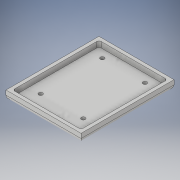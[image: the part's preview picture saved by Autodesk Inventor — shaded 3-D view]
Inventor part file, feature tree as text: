
AUTODESK INVENTOR PART (.ipt)
format: ipt  version: 2019.4 (Build 234330000, 330)  size: 144,384 bytes
history: native  units: mm
features: extrude x3, sketch x3, fillet x2
ambient origin geometry x8: Origin, YZ Plane, XZ Plane, XY Plane, X Axis, Y Axis, Z Axis, Center Point
bodies: Solid1 (feature_tree)
feature tree (8):
  extrude  "Extrusion1"  Depth=83.0mm
  extrude  "Extrusion2"  Depth=61.0mm
  extrude  "Extrusion3"  Depth=5.0mm TaperAngle=0.0deg
  fillet  "Fillet1"  Radius=3.5mm
  fillet  "Fillet2"  Radius=7.5mm
  sketch  "Sketch1"  dims[d0=67.0mm d1=83.0mm]
  sketch  "Sketch2"  dims[d2=3.0mm d3=0.0mm d4=61.0mm]
  sketch  "Sketch3"  dims[d5=77.0mm d6=5.0mm d7=0.0mm d8=3.5mm d9=7.5mm d10=12.5mm d11=20.0mm d13=55.0mm d14=20.0mm d16=38.0mm d19=5.0mm d20=0.0mm d21=4.0mm d22=2.0mm]
